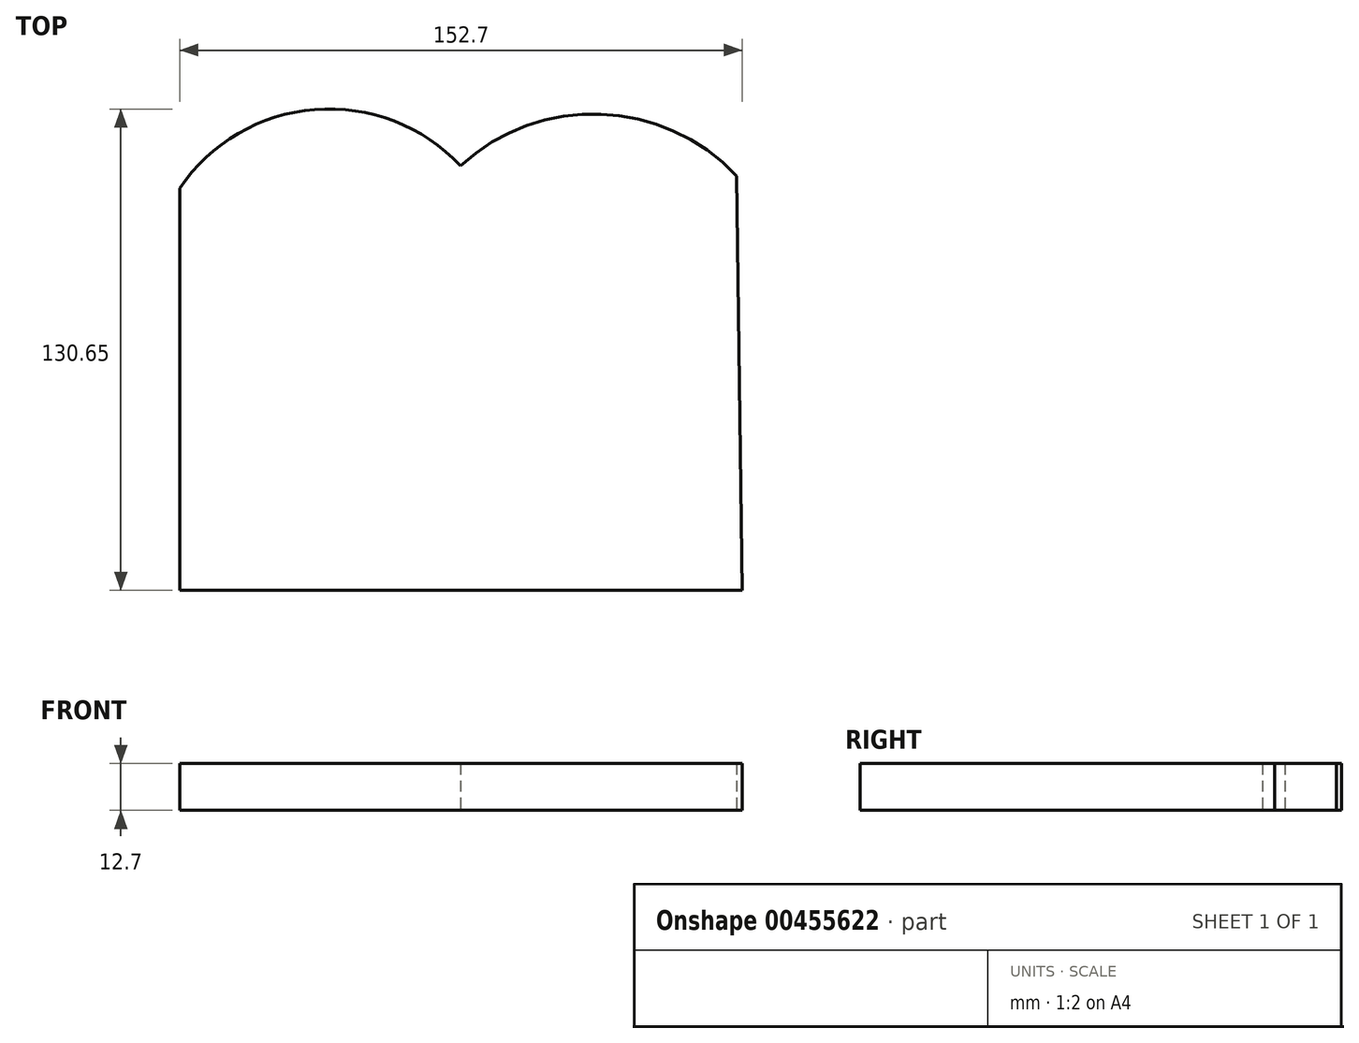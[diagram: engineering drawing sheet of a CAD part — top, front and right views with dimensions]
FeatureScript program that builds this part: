
annotation { "Feature Type Name" : "Feature", "Feature Type Description" : "" }
export const myFeature = defineFeature(function(context is Context, id is Id, definition is map)
    precondition{}
    {
        {
            var Q0;
            Q0=qCreatedBy(makeId("Top.planeOp"),FACE);
            var sketch = newSketch(context, id + "F0", { "sketchPlane" : qUnion([Q0])});
            skLineSegment(sketch, "E0", {"start": v(-76.2, 52.27) * mm, "end": v(-76.2, -56.85) * mm});
            skArc(sketch, "E1", {"start": v(0, 58.37) * mm, "mid": v(-39.57, 73.65) * mm, "end": v(-76.2, 52.27) * mm});
            skArc(sketch, "E2", {"start": v(74.98, 55.63) * mm, "mid": v(38.05, 72.4) * mm, "end": v(0, 58.37) * mm});
            skLineSegment(sketch, "E3", {"start": v(-76.2, -56.85) * mm, "end": v(76.5, -56.85) * mm});
            skLineSegment(sketch, "E4", {"start": v(76.5, -56.85) * mm, "end": v(74.98, 55.63) * mm});
            skSolve(sketch);
        }
        {
            var Q0;
            Q0=makeQuery(id+"F0.imprint","IMPRINT",FACE,{"disambiguationData":[TD([[makeQuery(id+"F0.imprint","IMPRINT",EDGE,{"derivedFrom":sQuery(id+"F0.wireOp",EDGE,"E0")}),1.0]])]});
            extrude(context, id + "F1", {"entities" : qUnion([Q0]), "depth" : 12.7 * mm});
        }
    });
